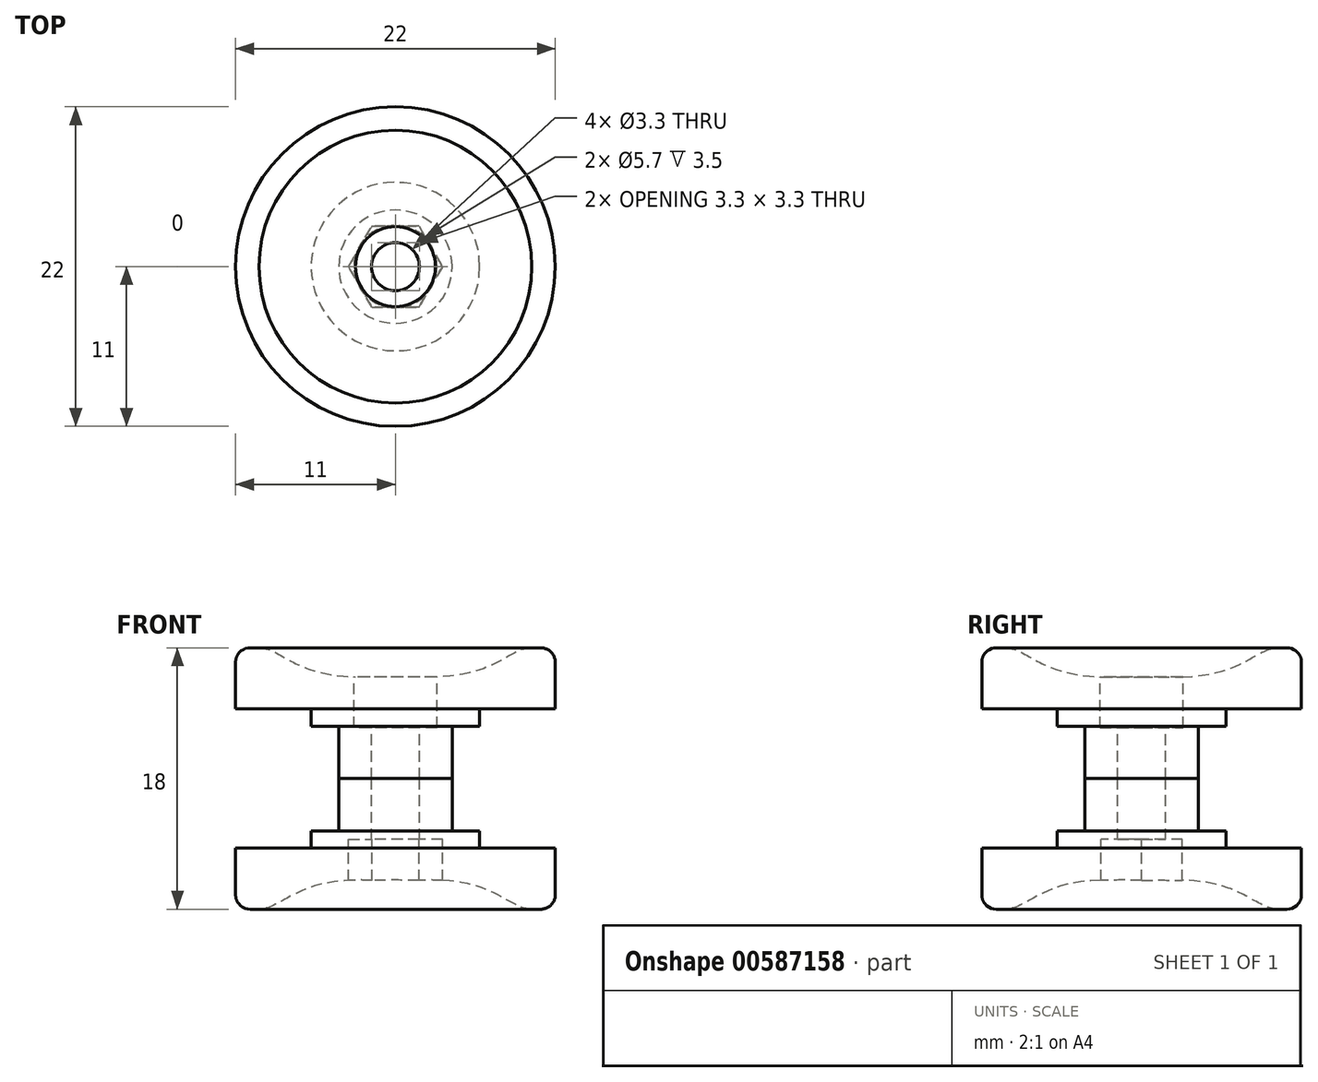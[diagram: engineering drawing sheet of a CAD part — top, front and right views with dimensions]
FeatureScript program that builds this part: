
annotation { "Feature Type Name" : "Feature", "Feature Type Description" : "" }
export const myFeature = defineFeature(function(context is Context, id is Id, definition is map)
    precondition{}
    {
        {
            var Q0;
            Q0=qCreatedBy(makeId("Front.planeOp"),FACE);
            var sketch = newSketch(context, id + "F0", { "sketchPlane" : qUnion([Q0])});
            skLineSegment(sketch, "E0", {"start": v(-3.9, 0) * mm, "end": v(-3.9, 3.6) * mm});
            skLineSegment(sketch, "E1", {"start": v(-3.9, 3.6) * mm, "end": v(-5.8, 3.6) * mm});
            skLineSegment(sketch, "E2", {"start": v(-5.8, 3.6) * mm, "end": v(-5.8, 4.8) * mm});
            skLineSegment(sketch, "E3", {"start": v(-5.8, 4.8) * mm, "end": v(-11, 4.8) * mm});
            skLineSegment(sketch, "E4", {"start": v(-11, 4.8) * mm, "end": v(-11, 8) * mm});
            skPoint(sketch, "E5.visualSharp", {"position": v(-11, 8) * mm});
            skArc(sketch, "E5.filletArc", {"start": v(-10, 9) * mm, "mid": v(-10.7, 8.7) * mm, "end": v(-11, 8) * mm});
            skLineSegment(sketch, "E6", {"start": v(0, 11.77) * mm, "end": v(0, -7.66) * mm});
            skLineSegment(sketch, "E7", {"start": v(-3.9, 0) * mm, "end": v(0, 0) * mm});
            skLineSegment(sketch, "E8", {"start": v(0, 7) * mm, "end": v(-2.75, 7) * mm});
            skLineSegment(sketch, "E9", {"start": v(-10, 9) * mm, "end": v(-9.39, 9) * mm});
            skFitSpline(sketch, "E10", {"points": [v(-9.39, 9) * mm, v(-2.75, 7) * mm], "startDerivative": vector(4.82, -0.15) * mm, "endDerivative": vector(12.52, -0.2) * mm});
            skLineSegment(sketch, "E11.MirrorCS", {"start": v(-3.9, -3.6) * mm, "end": v(-5.8, -3.6) * mm});
            skLineSegment(sketch, "E12.MirrorCS", {"start": v(-5.8, -4.8) * mm, "end": v(-11, -4.8) * mm});
            skLineSegment(sketch, "E13.MirrorCS", {"start": v(-3.9, 0) * mm, "end": v(-3.9, -3.6) * mm});
            skLineSegment(sketch, "E14.MirrorCS", {"start": v(-5.8, -3.6) * mm, "end": v(-5.8, -4.8) * mm});
            skLineSegment(sketch, "E15.MirrorCS", {"start": v(-11, -4.8) * mm, "end": v(-11, -8) * mm});
            skPoint(sketch, "E16.MirrorP", {"position": v(-11, -8) * mm});
            skFitSpline(sketch, "E17.MirrorCS", {"points": [v(-9.39, -9) * mm, v(-2.75, -7) * mm], "startDerivative": vector(4.82, 0.15) * mm, "endDerivative": vector(12.52, 0.2) * mm});
            skLineSegment(sketch, "E18.MirrorCS", {"start": v(-10, -9) * mm, "end": v(-9.39, -9) * mm});
            skLineSegment(sketch, "E19.MirrorCS", {"start": v(0, -7) * mm, "end": v(-2.75, -7) * mm});
            skArc(sketch, "E20.MirrorCS", {"start": v(-10, -9) * mm, "mid": v(-10.7, -8.7) * mm, "end": v(-11, -8) * mm});
            skSolve(sketch);
        }
        {
            var Q0;
            Q0=makeQuery(id+"F0.imprint","IMPRINT",FACE,{"disambiguationData":[TD([[makeQuery(id+"F0.imprint","IMPRINT",EDGE,{"derivedFrom":sQuery(id+"F0.wireOp",EDGE,"E0")}),-1.0]])]});
            var Q1;
            Q1=sQuery(id+"F0.wireOp",EDGE,"E6");
            revolve(context, id + "F1", {"entities" : qUnion([Q0]), "axis" : qUnion([Q1]), "revolveType" : RevolveType.FULL});
        }
        {
            var Q0;
            Q0=makeQuery(id+"F0.imprint","IMPRINT",FACE,{"disambiguationData":[TD([[makeQuery(id+"F0.imprint","IMPRINT",EDGE,{"derivedFrom":sQuery(id+"F0.wireOp",EDGE,"E11.MirrorCS")}),1.0]])]});
            var Q1;
            Q1=sQuery(id+"F0.wireOp",EDGE,"E6");
            revolve(context, id + "F2", {"entities" : qUnion([Q0]), "axis" : qUnion([Q1]), "revolveType" : RevolveType.FULL});
        }
        {
            var Q0;
            Q0=qCreatedBy(makeId("Top.planeOp"),FACE);
            cPlane(context, id + "F3", {"entities" : qUnion([Q0]), "cplaneType" : CPlaneType.OFFSET, "offset" : 7 * mm, "width" : 150 * mm, "height" : 150 * mm});
        }
        {
            var Q0;
            Q0=qCreatedBy(id+"F3.planeOp",FACE);
            var sketch = newSketch(context, id + "F4", { "sketchPlane" : qUnion([Q0])});
            skPoint(sketch, "E21", {"position": v(0, 0) * mm});
            skSolve(sketch);
        }
        {
            var Q0;
            Q0=sQuery(id+"F4.wireOp",VERTEX,"E21");
            var Q1;
            Q1=makeQuery(id+"F1.opRevolve","SWEPT_BODY",BODY,{"disambiguationData":[OSD([sQuery(id+"F0.wireOp",EDGE,"E0"),sQuery(id+"F0.wireOp",EDGE,"E1"),sQuery(id+"F0.wireOp",EDGE,"E2"),sQuery(id+"F0.wireOp",EDGE,"E3"),sQuery(id+"F0.wireOp",EDGE,"E4"),sQuery(id+"F0.wireOp",EDGE,"E5.filletArc"),sQuery(id+"F0.wireOp",EDGE,"6aba7e35-7b74-4366-8450-34e27a5a92db"),sQuery(id+"F0.wireOp",EDGE,"E6"),sQuery(id+"F0.wireOp",EDGE,"E7")])]});
            var Q2;
            Q2=makeQuery(id+"F2.opRevolve","SWEPT_BODY",BODY,{"disambiguationData":[OSD([sQuery(id+"F0.wireOp",EDGE,"E6"),sQuery(id+"F0.wireOp",EDGE,"f0027028-0b92-447f-8ecc-35d1badcfe532.MirrorCS"),sQuery(id+"F0.wireOp",EDGE,"f0027028-0b92-447f-8ecc-35d1badcfe533.MirrorCS"),sQuery(id+"F0.wireOp",EDGE,"E7"),sQuery(id+"F0.wireOp",EDGE,"f0027028-0b92-447f-8ecc-35d1badcfe535.MirrorCS"),sQuery(id+"F0.wireOp",EDGE,"f0027028-0b92-447f-8ecc-35d1badcfe536.MirrorCS"),sQuery(id+"F0.wireOp",EDGE,"f0027028-0b92-447f-8ecc-35d1badcfe537.MirrorCS"),sQuery(id+"F0.wireOp",EDGE,"f0027028-0b92-447f-8ecc-35d1badcfe538.MirrorCS"),sQuery(id+"F0.wireOp",EDGE,"f0027028-0b92-447f-8ecc-35d1badcfe539.MirrorCS")])]});
            hole(context, id + "F5", {"style" : HoleStyle.C_BORE, "endStyle" : HoleEndStyle.BLIND, "holeDiameter" : 3.3 * mm, "cBoreDiameter" : 5.7 * mm, "cBoreDepth" : 3.5 * mm, "majorDiameter" : 5 * mm, "holeDepth" : 14.4 * mm, "isTappedThrough" : true, "tappedDepth" : 12 * mm, "tapClearance" : 3, "startFromSketch" : true, "locations" : qUnion([Q0]), "scope" : qUnion([Q1, Q2])});
        }
        {
            var Q0;
            Q0=qCreatedBy(makeId("Top.planeOp"),FACE);
            cPlane(context, id + "F6", {"entities" : qUnion([Q0]), "cplaneType" : CPlaneType.OFFSET, "offset" : 6.5 * mm, "oppositeDirection" : true, "width" : 150 * mm, "height" : 150 * mm});
        }
        {
            var Q0;
            Q0=qCreatedBy(id+"F6.planeOp",FACE);
            var sketch = newSketch(context, id + "F7", { "sketchPlane" : qUnion([Q0])});
            skCircle(sketch, "E22.cCircle", {"center": v(0, 0) * mm, "radius": 2.8 * mm, "construction": true});
            skLineSegment(sketch, "E22.0", {"start": v(1.62, -2.8) * mm, "end": v(-1.62, -2.8) * mm});
            skLineSegment(sketch, "E22.1", {"start": v(-1.62, -2.8) * mm, "end": v(-3.23, 0) * mm});
            skLineSegment(sketch, "E22.2", {"start": v(-3.23, 0) * mm, "end": v(-1.62, 2.8) * mm});
            skLineSegment(sketch, "E22.3", {"start": v(-1.62, 2.8) * mm, "end": v(1.62, 2.8) * mm});
            skLineSegment(sketch, "E22.4", {"start": v(1.62, 2.8) * mm, "end": v(3.23, 0) * mm});
            skLineSegment(sketch, "E22.5", {"start": v(3.23, 0) * mm, "end": v(1.62, -2.8) * mm});
            skPoint(sketch, "E22.0.midPoint", {"position": v(0, -2.8) * mm});
            skSolve(sketch);
        }
        {
            var Q0;
            Q0 = qSketchRegion(id + "F7", true);
            extrude(context, id + "F8", {"entities" : qUnion([Q0]), "operationType" : NewBodyOperationType.REMOVE, "endBound" : BoundingType.SYMMETRIC, "oppositeDirection" : true, "depth" : 4.6 * mm, "offsetDistance" : 25 * mm});
        }
    });
